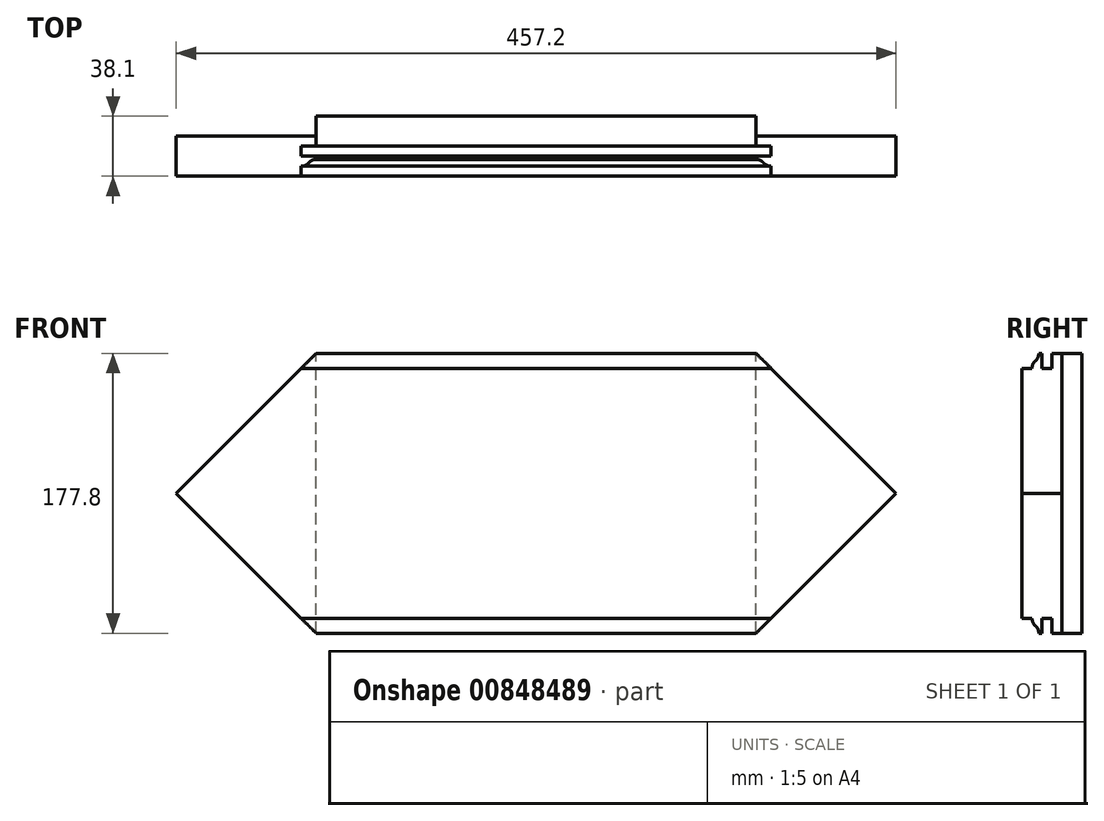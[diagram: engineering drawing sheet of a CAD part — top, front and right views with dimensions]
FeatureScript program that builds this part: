
annotation { "Feature Type Name" : "Feature", "Feature Type Description" : "" }
export const myFeature = defineFeature(function(context is Context, id is Id, definition is map)
    precondition{}
    {
        {
            var Q0;
            Q0=qCreatedBy(makeId("Front.planeOp"),FACE);
            var sketch = newSketch(context, id + "F0", { "sketchPlane" : qUnion([Q0])});
            skLineSegment(sketch, "E0.bottom", {"start": v(-228.6, 44.45) * mm, "end": v(228.6, 44.45) * mm});
            skLineSegment(sketch, "E0.top", {"start": v(-228.6, -44.45) * mm, "end": v(228.6, -44.45) * mm});
            skLineSegment(sketch, "E0.left", {"start": v(-228.6, 44.45) * mm, "end": v(-228.6, -44.45) * mm});
            skLineSegment(sketch, "E0.right", {"start": v(228.6, 44.45) * mm, "end": v(228.6, -44.45) * mm});
            skPoint(sketch, "E0.middle", {"position": v(0, 0) * mm});
            skSolve(sketch);
        }
        {
            var Q0;
            Q0=qSketchRegion(id+"F0",true);
            extrude(context, id + "F1", {"entities" : qUnion([Q0]), "oppositeDirection" : true, "depth" : 38.1 * mm, "offsetDistance" : 25.4 * mm});
        }
        {
            var Q0;
            Q0=makeQuery(id+"F1.opExtrude","SWEPT_FACE",FACE,{"disambiguationData":[OSD([sQuery(id+"F0.wireOp",EDGE,"E0.right")])]});
            var sketch = newSketch(context, id + "F2", { "sketchPlane" : qUnion([Q0])});
            skLineSegment(sketch, "E1", {"start": v(22.22, -38.1) * mm, "end": v(19.05, -44.45) * mm});
            skLineSegment(sketch, "E2", {"start": v(31.75, -44.45) * mm, "end": v(28.57, -38.1) * mm});
            skLineSegment(sketch, "E3", {"start": v(22.22, -38.1) * mm, "end": v(28.57, -38.1) * mm});
            skLineSegment(sketch, "E4", {"start": v(31.75, -44.45) * mm, "end": v(19.05, -44.45) * mm});
            skSolve(sketch);
        }
        {
            var Q0;
            Q0=makeQuery(id+"F1.opExtrude","SWEPT_FACE",FACE,{"disambiguationData":[OSD([sQuery(id+"F0.wireOp",EDGE,"E0.right")])]});
            var sketch = newSketch(context, id + "F3", { "sketchPlane" : qUnion([Q0])});
            skLineSegment(sketch, "E5", {"start": v(0, 34.93) * mm, "end": v(6.35, 34.93) * mm});
            skLineSegment(sketch, "E6", {"start": v(12.7, 34.93) * mm, "end": v(19.05, 34.93) * mm});
            skArc(sketch, "E7", {"start": v(8.5, 39.69) * mm, "mid": v(6.91, 37.54) * mm, "end": v(6.35, 34.93) * mm});
            skLineSegment(sketch, "E8", {"start": v(12.7, 44.45) * mm, "end": v(12.7, 34.93) * mm});
            skLineSegment(sketch, "E9", {"start": v(19.05, 34.93) * mm, "end": v(19.05, 44.45) * mm});
            skLineSegment(sketch, "E10", {"start": v(10.65, 44.45) * mm, "end": v(0, 44.45) * mm});
            skLineSegment(sketch, "E11", {"start": v(0, 44.45) * mm, "end": v(0, 34.93) * mm});
            skLineSegment(sketch, "E12", {"start": v(12.7, 44.45) * mm, "end": v(19.05, 44.45) * mm});
            skArc(sketch, "E13", {"start": v(8.5, 39.69) * mm, "mid": v(10.09, 41.84) * mm, "end": v(10.65, 44.45) * mm});
            skSolve(sketch);
        }
        {
            var Q0;
            Q0=qSketchRegion(id+"F3",true);
            extrude(context, id + "F4", {"entities" : qUnion([Q0]), "operationType" : NewBodyOperationType.REMOVE, "endBound" : BoundingType.THROUGH_ALL, "oppositeDirection" : true, "depth" : 25.4 * mm, "offsetDistance" : 25.4 * mm});
        }
        {
            var Q0;
            Q0=makeQuery(id+"F1.opExtrude","CAP_FACE",FACE,{"disambiguationData":[OSD([sQuery(id+"F0.wireOp",EDGE,"E0.bottom"),sQuery(id+"F0.wireOp",EDGE,"E0.top"),sQuery(id+"F0.wireOp",EDGE,"E0.left"),sQuery(id+"F0.wireOp",EDGE,"E0.right")])],"isStart":true});
            var sketch = newSketch(context, id + "F5", { "sketchPlane" : qUnion([Q0])});
            skLineSegment(sketch, "E14", {"start": v(-228.6, -44.45) * mm, "end": v(-139.7, 44.45) * mm});
            skLineSegment(sketch, "E15", {"start": v(-139.7, 44.45) * mm, "end": v(-228.6, 44.45) * mm});
            skLineSegment(sketch, "E16", {"start": v(-228.6, 44.45) * mm, "end": v(-228.6, -44.45) * mm});
            skPoint(sketch, "E17", {"position": v(-228.6, -4.76) * mm});
            skLineSegment(sketch, "E18", {"start": v(0, 760.27) * mm, "end": v(0, -577.9) * mm, "construction": true});
            skLineSegment(sketch, "E19.MirrorCS", {"start": v(228.6, 44.45) * mm, "end": v(228.6, -44.45) * mm});
            skLineSegment(sketch, "E20.MirrorCS", {"start": v(228.6, -44.45) * mm, "end": v(139.7, 44.45) * mm});
            skLineSegment(sketch, "E21.MirrorCS", {"start": v(139.7, 44.45) * mm, "end": v(228.6, 44.45) * mm});
            skSolve(sketch);
        }
        {
            var Q0;
            Q0=qSketchRegion(id+"F5",true);
            extrude(context, id + "F6", {"entities" : qUnion([Q0]), "operationType" : NewBodyOperationType.REMOVE, "oppositeDirection" : true, "depth" : 25.4 * mm, "offsetDistance" : 25.4 * mm});
        }
        {
            var Q0;
            {var subQ2=sQuery(id+"F0.wireOp",EDGE,"E0.bottom");Q0=makeQuery(id+"F4.boolean.opBoolean","SPLIT",FACE,{"disambiguationData":[TD([makeQuery(id+"F4.opExtrude","SWEPT_FACE",FACE,{"disambiguationData":[OSD([sQuery(id+"F3.wireOp",EDGE,"E9")])]})])],"derivedFrom":makeQuery(id+"F1.opExtrude","SWEPT_FACE",FACE,{"disambiguationData":[OSD([subQ2])]})});}
            var sketch = newSketch(context, id + "F7", { "sketchPlane" : qUnion([Q0])});
            skLineSegment(sketch, "E22.bottom", {"start": v(-228.6, 38.1) * mm, "end": v(-139.7, 38.1) * mm});
            skLineSegment(sketch, "E22.top", {"start": v(-228.6, 25.4) * mm, "end": v(-139.7, 25.4) * mm});
            skLineSegment(sketch, "E22.left", {"start": v(-228.6, 38.1) * mm, "end": v(-228.6, 25.4) * mm});
            skLineSegment(sketch, "E22.right", {"start": v(-139.7, 38.1) * mm, "end": v(-139.7, 25.4) * mm});
            skLineSegment(sketch, "E23", {"start": v(0, 107.05) * mm, "end": v(0, -115.05) * mm, "construction": true});
            skLineSegment(sketch, "E24.MirrorCS", {"start": v(228.6, 38.1) * mm, "end": v(139.7, 38.1) * mm});
            skLineSegment(sketch, "E25.MirrorCS", {"start": v(228.6, 38.1) * mm, "end": v(228.6, 25.4) * mm});
            skLineSegment(sketch, "E26.MirrorCS", {"start": v(228.6, 25.4) * mm, "end": v(139.7, 25.4) * mm});
            skLineSegment(sketch, "E27.MirrorCS", {"start": v(139.7, 38.1) * mm, "end": v(139.7, 25.4) * mm});
            skSolve(sketch);
        }
        {
            var Q0;
            Q0=qSketchRegion(id+"F7",true);
            extrude(context, id + "F8", {"entities" : qUnion([Q0]), "operationType" : NewBodyOperationType.REMOVE, "endBound" : BoundingType.UP_TO_NEXT, "oppositeDirection" : true, "depth" : 25.4 * mm, "offsetDistance" : 25.4 * mm});
        }
        {
            var Q0;
            Q0=makeQuery(id+"F1.opExtrude","SWEPT_BODY",BODY,{"disambiguationData":[OSD([sQuery(id+"F0.wireOp",EDGE,"E0.bottom"),sQuery(id+"F0.wireOp",EDGE,"E0.top"),sQuery(id+"F0.wireOp",EDGE,"E0.left"),sQuery(id+"F0.wireOp",EDGE,"E0.right")])]});
            var Q1;
            Q1=makeQuery(id+"F1.opExtrude","SWEPT_FACE",FACE,{"disambiguationData":[OSD([sQuery(id+"F0.wireOp",EDGE,"E0.top")])]});
            mirror(context, id + "F9", {"operationType" : NewBodyOperationType.ADD, "entities" : qUnion([Q0]), "mirrorPlane" : qUnion([Q1])});
        }
    });
